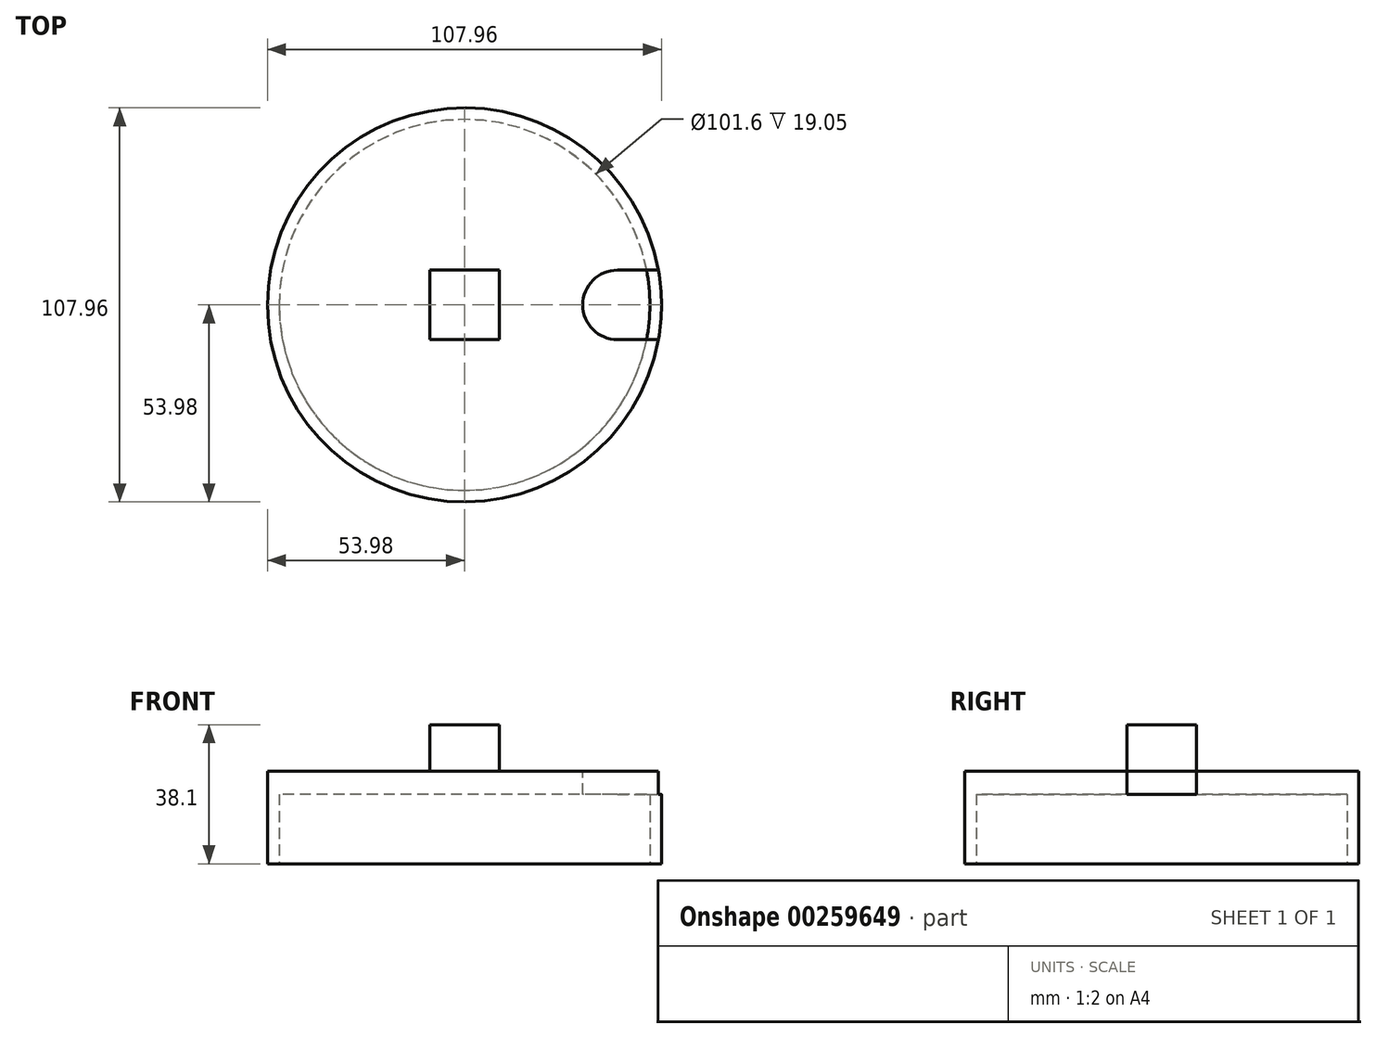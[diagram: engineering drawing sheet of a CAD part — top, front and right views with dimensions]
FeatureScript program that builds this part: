
annotation { "Feature Type Name" : "Feature", "Feature Type Description" : "" }
export const myFeature = defineFeature(function(context is Context, id is Id, definition is map)
    precondition{}
    {
        {
            var Q0;
            Q0=qCreatedBy(makeId("Top.planeOp"),FACE);
            var sketch = newSketch(context, id + "F0", { "sketchPlane" : qUnion([Q0])});
            skCircle(sketch, "E0", {"center": v(0, 0) * mm, "radius": 53.98 * mm});
            skSolve(sketch);
        }
        {
            var Q0;
            Q0 = qSketchRegion(id + "F0", true);
            extrude(context, id + "F1", {"entities" : qUnion([Q0]), "depth" : 25.4 * mm});
        }
        {
            var Q0;
            Q0=makeQuery(id+"F1.opExtrude","CAP_FACE",FACE,{"disambiguationData":[OSD([sQuery(id+"F0.wireOp",EDGE,"E0")])],"isStart":true});
            var sketch = newSketch(context, id + "F2", { "sketchPlane" : qUnion([Q0])});
            skCircle(sketch, "E1", {"center": v(0, 0) * mm, "radius": 50.8 * mm});
            skSolve(sketch);
        }
        {
            var Q0;
            Q0 = qSketchRegion(id + "F2", true);
            extrude(context, id + "F3", {"entities" : qUnion([Q0]), "operationType" : NewBodyOperationType.REMOVE, "oppositeDirection" : true, "depth" : 19.05 * mm});
        }
        {
            var Q0;
            Q0=makeQuery(id+"F1.opExtrude","CAP_FACE",FACE,{"disambiguationData":[OSD([sQuery(id+"F0.wireOp",EDGE,"E0")])],"isStart":false});
            var sketch = newSketch(context, id + "F4", { "sketchPlane" : qUnion([Q0])});
            skLineSegment(sketch, "E2.bottom", {"start": v(9.53, -9.52) * mm, "end": v(-9.53, -9.53) * mm});
            skLineSegment(sketch, "E2.top", {"start": v(9.53, 9.53) * mm, "end": v(-9.53, 9.52) * mm});
            skLineSegment(sketch, "E2.left", {"start": v(9.53, -9.52) * mm, "end": v(9.53, 9.53) * mm});
            skLineSegment(sketch, "E2.right", {"start": v(-9.53, -9.53) * mm, "end": v(-9.53, 9.52) * mm});
            skPoint(sketch, "E2.middle", {"position": v(0, 0) * mm});
            skSolve(sketch);
        }
        {
            var Q0;
            Q0 = qSketchRegion(id + "F4", true);
            extrude(context, id + "F5", {"entities" : qUnion([Q0]), "operationType" : NewBodyOperationType.ADD, "depth" : 12.7 * mm});
        }
        {
            var Q0;
            Q0=makeQuery(id+"F1.opExtrude","CAP_FACE",FACE,{"disambiguationData":[OSD([sQuery(id+"F0.wireOp",EDGE,"E0")])],"isStart":false});
            var sketch = newSketch(context, id + "F6", { "sketchPlane" : qUnion([Q0])});
            skCircle(sketch, "E3", {"center": v(41.91, 0) * mm, "radius": 9.53 * mm});
            skLineSegment(sketch, "E4", {"start": v(41.91, 0) * mm, "end": v(53.98, 0) * mm, "construction": true});
            skSolve(sketch);
        }
        {
            var Q0;
            Q0 = qSketchRegion(id + "F6", true);
            var Q1;
            Q1=makeQuery(id+"F3.boolean.opBoolean","COPY",FACE,{"derivedFrom":makeQuery(id+"F3.opExtrude","CAP_FACE",FACE,{"disambiguationData":[OSD([sQuery(id+"F2.wireOp",EDGE,"E1")])],"isStart":false})});
            extrude(context, id + "F7", {"entities" : qUnion([Q0]), "operationType" : NewBodyOperationType.REMOVE, "endBound" : BoundingType.UP_TO_SURFACE, "oppositeDirection" : true, "endBoundEntityFace" : qUnion([Q1]), "depth" : 6.35 * mm});
        }
        {
            var Q0;
            Q0=makeQuery(id+"F1.opExtrude","CAP_FACE",FACE,{"disambiguationData":[OSD([sQuery(id+"F0.wireOp",EDGE,"E0")])],"isStart":false});
            var sketch = newSketch(context, id + "F8", { "sketchPlane" : qUnion([Q0])});
            skLineSegment(sketch, "E5.bottom", {"start": v(41.91, 9.53) * mm, "end": v(59.03, 9.53) * mm});
            skLineSegment(sketch, "E5.top", {"start": v(41.91, -9.53) * mm, "end": v(59.03, -9.53) * mm});
            skLineSegment(sketch, "E5.left", {"start": v(41.91, 9.52) * mm, "end": v(41.91, -9.53) * mm});
            skLineSegment(sketch, "E5.right", {"start": v(59.03, 9.53) * mm, "end": v(59.03, -9.53) * mm});
            skSolve(sketch);
        }
        {
            var Q0;
            Q0 = qSketchRegion(id + "F8", true);
            var Q1;
            Q1=makeQuery(id+"F3.boolean.opBoolean","COPY",FACE,{"derivedFrom":makeQuery(id+"F3.opExtrude","CAP_FACE",FACE,{"disambiguationData":[OSD([sQuery(id+"F2.wireOp",EDGE,"E1")])],"isStart":false})});
            extrude(context, id + "F9", {"entities" : qUnion([Q0]), "operationType" : NewBodyOperationType.REMOVE, "endBound" : BoundingType.UP_TO_SURFACE, "oppositeDirection" : true, "endBoundEntityFace" : qUnion([Q1]), "depth" : 25.4 * mm});
        }
    });
